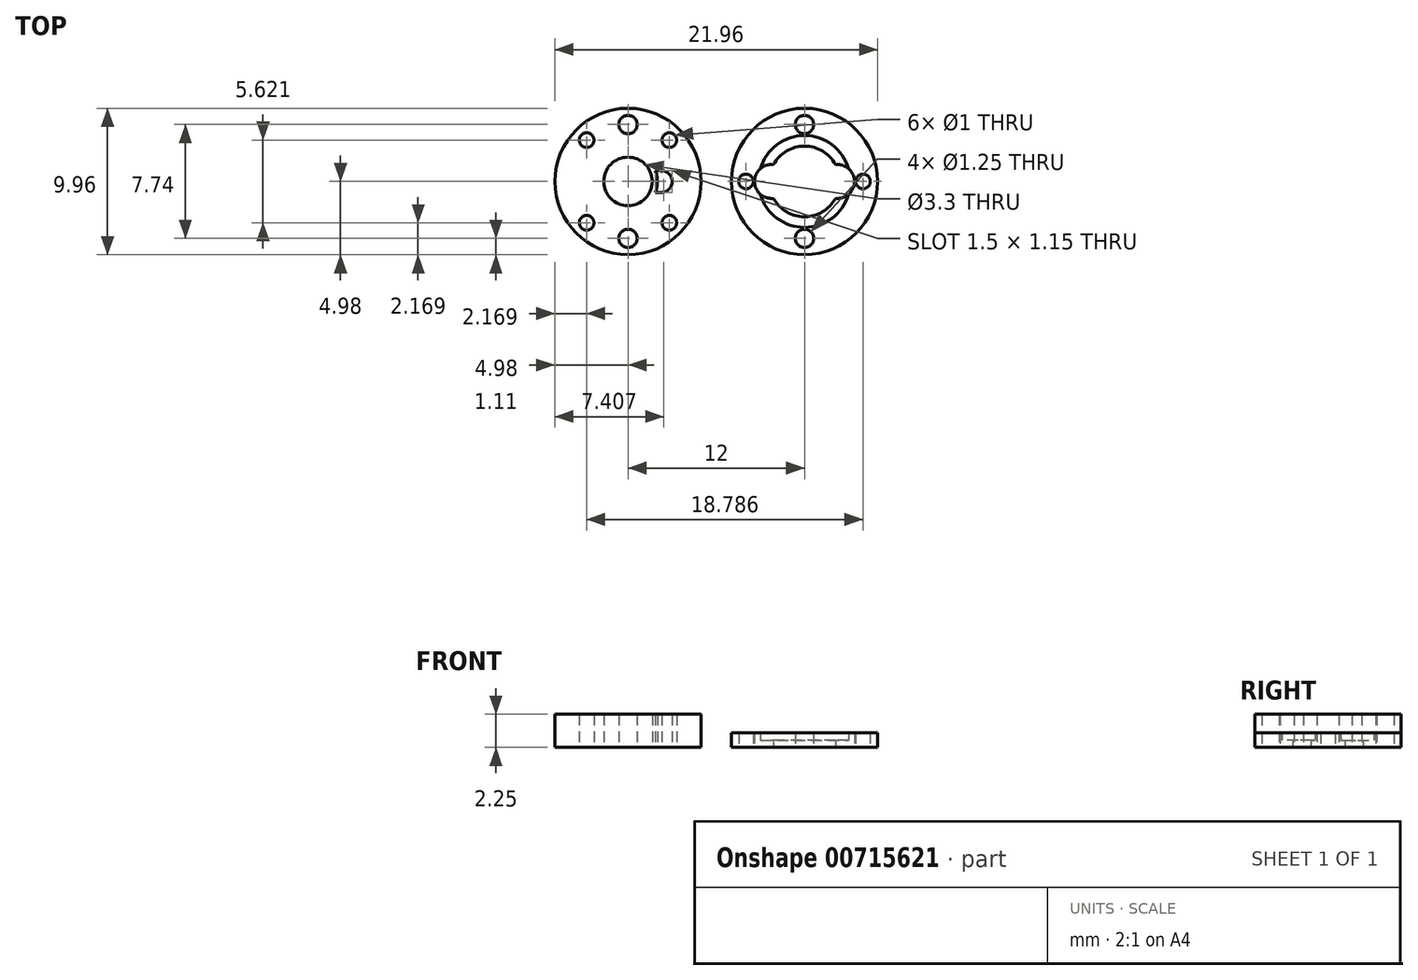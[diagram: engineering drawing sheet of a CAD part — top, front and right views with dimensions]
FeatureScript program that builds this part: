
annotation { "Feature Type Name" : "Feature", "Feature Type Description" : "" }
export const myFeature = defineFeature(function(context is Context, id is Id, definition is map)
    precondition{}
    {
        {
            var Q0;
            Q0=qCreatedBy(makeId("Top.planeOp"),FACE);
            var sketch = newSketch(context, id + "F0", { "sketchPlane" : qUnion([Q0])});
            skCircle(sketch, "E0", {"center": v(0, 0) * mm, "radius": 4.98 * mm});
            skCircle(sketch, "E1", {"center": v(0, 0) * mm, "radius": 1.65 * mm});
            skLineSegment(sketch, "E2", {"start": v(0, 0) * mm, "end": v(-3, 0) * mm, "construction": true});
            skLineSegment(sketch, "E3", {"start": v(0, 0.75) * mm, "end": v(0, 6.53) * mm, "construction": true});
            skLineSegment(sketch, "E4.bottom", {"start": v(-2.25, -0.75) * mm, "end": v(-1.99, -0.75) * mm});
            skLineSegment(sketch, "E4.top", {"start": v(-2.25, 0.75) * mm, "end": v(-1.99, 0.75) * mm});
            skLineSegment(sketch, "E4.left", {"start": v(-3, 0) * mm, "end": v(-3, 0) * mm});
            skLineSegment(sketch, "E4.right", {"start": v(0, 0) * mm, "end": v(0, 0.75) * mm});
            skPoint(sketch, "E4.middle", {"position": v(-1.5, 0) * mm});
            skPoint(sketch, "E5.orphan", {"position": v(0, -0.75) * mm});
            skPoint(sketch, "E6.visualSharp", {"position": v(-3, 0.75) * mm});
            skArc(sketch, "E6.filletArc", {"start": v(-2.25, 0.75) * mm, "mid": v(-2.78, 0.53) * mm, "end": v(-3, 0) * mm});
            skPoint(sketch, "E7.visualSharp", {"position": v(-3, -0.75) * mm});
            skArc(sketch, "E7.filletArc", {"start": v(-3, 0) * mm, "mid": v(-2.78, -0.53) * mm, "end": v(-2.25, -0.75) * mm});
            skArc(sketch, "E8.MirrorCS", {"start": v(3, 0) * mm, "mid": v(2.78, -0.53) * mm, "end": v(2.25, -0.75) * mm});
            skLineSegment(sketch, "E9.MirrorCS", {"start": v(2.25, -0.75) * mm, "end": v(1.99, -0.75) * mm});
            skArc(sketch, "E10.MirrorCS", {"start": v(2.25, 0.75) * mm, "mid": v(2.78, 0.53) * mm, "end": v(3, 0) * mm});
            skLineSegment(sketch, "E11.MirrorCS", {"start": v(2.25, 0.75) * mm, "end": v(1.99, 0.75) * mm});
            skLineSegment(sketch, "E12", {"start": v(0, 4.98) * mm, "end": v(0, 3.87) * mm, "construction": true});
            skCircle(sketch, "E13", {"center": v(0, 3.87) * mm, "radius": 0.62 * mm});
            skCircle(sketch, "E14.1.0", {"center": v(0, -3.87) * mm, "radius": 0.62 * mm});
            skLineSegment(sketch, "E15", {"start": v(0, 0) * mm, "end": v(-3.52, 3.52) * mm, "construction": true});
            skLineSegment(sketch, "E16", {"start": v(-3.52, 3.52) * mm, "end": v(-2.81, 2.81) * mm, "construction": true});
            skCircle(sketch, "E17", {"center": v(-2.81, 2.81) * mm, "radius": 0.5 * mm});
            skLineSegment(sketch, "E18.MirrorCS", {"start": v(0, 0) * mm, "end": v(-3.52, -3.52) * mm, "construction": true});
            skCircle(sketch, "E19.MirrorC", {"center": v(-2.81, -2.81) * mm, "radius": 0.5 * mm});
            skLineSegment(sketch, "E20.MirrorCS", {"start": v(-3.52, -3.52) * mm, "end": v(-2.81, -2.81) * mm, "construction": true});
            skCircle(sketch, "E21.MirrorC", {"center": v(2.81, 2.81) * mm, "radius": 0.5 * mm});
            skCircle(sketch, "E22.MirrorC", {"center": v(2.81, -2.81) * mm, "radius": 0.5 * mm});
            skLineSegment(sketch, "E23", {"start": v(0, 0) * mm, "end": v(12, 0) * mm, "construction": true});
            skCircle(sketch, "E24", {"center": v(12, 0) * mm, "radius": 4.97 * mm});
            skArc(sketch, "E25", {"start": v(10.15, -0.75) * mm, "mid": v(12, -2) * mm, "end": v(13.85, -0.75) * mm, "construction": true});
            skCircle(sketch, "E26", {"center": v(12, 0) * mm, "radius": 3.12 * mm});
            skLineSegment(sketch, "E27", {"start": v(12, 0) * mm, "end": v(15, 0) * mm, "construction": true});
            skLineSegment(sketch, "E28.bottom", {"start": v(13.85, -0.75) * mm, "end": v(14.25, -0.75) * mm, "construction": true});
            skLineSegment(sketch, "E28.top", {"start": v(13.85, 0.75) * mm, "end": v(14.25, 0.75) * mm, "construction": true});
            skLineSegment(sketch, "E28.left", {"start": v(12, -0.75) * mm, "end": v(12, 0.75) * mm});
            skLineSegment(sketch, "E28.right", {"start": v(15, -0.75) * mm, "end": v(15, 0) * mm, "construction": true});
            skPoint(sketch, "E28.middle", {"position": v(13.5, 0) * mm});
            skPoint(sketch, "E29.visualSharp", {"position": v(15, 0.75) * mm});
            skArc(sketch, "E29.filletArc", {"start": v(15, 0) * mm, "mid": v(14.78, 0.53) * mm, "end": v(14.25, 0.75) * mm, "construction": true});
            skArc(sketch, "E30.MirrorCS", {"start": v(15, 0) * mm, "mid": v(14.78, -0.53) * mm, "end": v(14.25, -0.75) * mm, "construction": true});
            skLineSegment(sketch, "E31.MirrorCS", {"start": v(10.15, -0.75) * mm, "end": v(9.75, -0.75) * mm, "construction": true});
            skArc(sketch, "E32.MirrorCS", {"start": v(9, 0) * mm, "mid": v(9.22, -0.53) * mm, "end": v(9.75, -0.75) * mm, "construction": true});
            skArc(sketch, "E33.MirrorCS", {"start": v(9, 0) * mm, "mid": v(9.22, 0.53) * mm, "end": v(9.75, 0.75) * mm, "construction": true});
            skLineSegment(sketch, "E34.MirrorCS", {"start": v(10.15, 0.75) * mm, "end": v(9.75, 0.75) * mm, "construction": true});
            skArc(sketch, "E35.trimOffspring", {"start": v(13.85, 0.75) * mm, "mid": v(12, 2) * mm, "end": v(10.15, 0.75) * mm, "construction": true});
            skLineSegment(sketch, "E36.0", {"start": v(14.1, 1.15) * mm, "end": v(14.25, 1.15) * mm});
            skArc(sketch, "E36.1", {"start": v(15.4, 0) * mm, "mid": v(15.06, 0.81) * mm, "end": v(14.25, 1.15) * mm});
            skArc(sketch, "E36.2", {"start": v(14.1, 1.15) * mm, "mid": v(12, 2.4) * mm, "end": v(9.9, 1.15) * mm});
            skArc(sketch, "E36.3", {"start": v(15.4, 0) * mm, "mid": v(15.06, -0.81) * mm, "end": v(14.25, -1.15) * mm});
            skLineSegment(sketch, "E36.4", {"start": v(14.1, -1.15) * mm, "end": v(14.25, -1.15) * mm});
            skArc(sketch, "E36.5", {"start": v(9.9, -1.15) * mm, "mid": v(12, -2.4) * mm, "end": v(14.1, -1.15) * mm});
            skLineSegment(sketch, "E36.6", {"start": v(9.9, 1.15) * mm, "end": v(9.75, 1.15) * mm});
            skArc(sketch, "E36.7", {"start": v(8.6, 0) * mm, "mid": v(8.94, 0.81) * mm, "end": v(9.75, 1.15) * mm});
            skArc(sketch, "E36.8", {"start": v(8.6, 0) * mm, "mid": v(8.94, -0.81) * mm, "end": v(9.75, -1.15) * mm});
            skLineSegment(sketch, "E36.9", {"start": v(9.9, -1.15) * mm, "end": v(9.75, -1.15) * mm});
            skLineSegment(sketch, "E37", {"start": v(12, 4.97) * mm, "end": v(12, 3.87) * mm, "construction": true});
            skCircle(sketch, "E38", {"center": v(12, 3.87) * mm, "radius": 0.62 * mm});
            skCircle(sketch, "E39.MirrorC", {"center": v(12, -3.87) * mm, "radius": 0.62 * mm});
            skLineSegment(sketch, "E40", {"start": v(12, 0) * mm, "end": v(7.03, 0) * mm, "construction": true});
            skLineSegment(sketch, "E41", {"start": v(7.03, 0) * mm, "end": v(8.03, 0) * mm, "construction": true});
            skCircle(sketch, "E42", {"center": v(8.03, 0) * mm, "radius": 0.5 * mm});
            skCircle(sketch, "E43.MirrorC", {"center": v(15.97, 0) * mm, "radius": 0.5 * mm});
            skCircle(sketch, "E44", {"center": v(0, 0) * mm, "radius": 2 * mm});
            skLineSegment(sketch, "E45", {"start": v(-2.25, 0.75) * mm, "end": v(-1.85, 0.75) * mm});
            skLineSegment(sketch, "E46", {"start": v(-2.25, -0.75) * mm, "end": v(-1.85, -0.75) * mm});
            skLineSegment(sketch, "E47", {"start": v(2.25, -0.75) * mm, "end": v(1.85, -0.75) * mm});
            skLineSegment(sketch, "E48", {"start": v(2.25, 0.75) * mm, "end": v(1.85, 0.75) * mm});
            skSolve(sketch);
        }
        {
            var Q0;
            Q0=makeQuery(id+"F0.imprint","IMPRINT",FACE,{"disambiguationData":[TD([[makeQuery(id+"F0.imprint","IMPRINT",EDGE,{"derivedFrom":sQuery(id+"F0.wireOp",EDGE,"E0")}),1.0]])]});
            extrude(context, id + "F1", {"entities" : qUnion([Q0]), "depth" : 1 * mm, "offsetDistance" : 25 * mm});
        }
        {
            var Q0;
            Q0=makeQuery(id+"F0.imprint","IMPRINT",FACE,{"disambiguationData":[TD([[makeQuery(id+"F0.imprint","IMPRINT",EDGE,{"derivedFrom":sQuery(id+"F0.wireOp",EDGE,"E8.MirrorCS")}),-1.0]])]});
            var Q1;
            Q1=makeQuery(id+"F0.imprint","IMPRINT",FACE,{"disambiguationData":[TD([[makeQuery(id+"F0.imprint","IMPRINT",EDGE,{"derivedFrom":sQuery(id+"F0.wireOp",EDGE,"E1")}),-1.0]])]});
            var Q2;
            {var subQ1=sQuery(id+"F0.wireOp",EDGE,"E4.bottom");Q2=makeQuery(id+"F0.imprint","IMPRINT",FACE,{"disambiguationData":[TD([[makeQuery(id+"F0.imprint","IMPRINT",EDGE,{"derivedFrom":subQ1}),1.0]])]});}
            var Q3;
            {var subQ1=sQuery(id+"F0.wireOp",EDGE,"E6.filletArc");Q3=makeQuery(id+"F0.imprint","IMPRINT",FACE,{"disambiguationData":[TD([[makeQuery(id+"F0.imprint","IMPRINT",EDGE,{"derivedFrom":subQ1}),1.0]])]});}
            extrude(context, id + "F2", {"entities" : qUnion([Q0, Q1, Q2, Q3]), "operationType" : NewBodyOperationType.ADD, "depth" : 2.25 * mm, "offsetDistance" : 25 * mm});
        }
        {
            var Q0;
            Q0=makeQuery(id+"F0.imprint","IMPRINT",FACE,{"disambiguationData":[TD([[makeQuery(id+"F0.imprint","IMPRINT",EDGE,{"derivedFrom":sQuery(id+"F0.wireOp",EDGE,"E24")}),1.0]])]});
            extrude(context, id + "F3", {"entities" : qUnion([Q0]), "depth" : 1 * mm, "offsetDistance" : 25 * mm});
        }
        {
            var Q0;
            {var subQ0=sQuery(id+"F0.wireOp",EDGE,"E36.4");Q0=makeQuery(id+"F0.imprint","IMPRINT",FACE,{"disambiguationData":[TD([[makeQuery(id+"F0.imprint","IMPRINT",EDGE,{"derivedFrom":subQ0}),-1.0]])]});}
            var Q1;
            {var subQ1=sQuery(id+"F0.wireOp",EDGE,"E36.0");Q1=makeQuery(id+"F0.imprint","IMPRINT",FACE,{"disambiguationData":[TD([[makeQuery(id+"F0.imprint","IMPRINT",EDGE,{"derivedFrom":subQ1}),1.0]])]});}
            extrude(context, id + "F4", {"entities" : qUnion([Q0, Q1]), "operationType" : NewBodyOperationType.ADD, "depth" : .5 * mm, "offsetDistance" : 25 * mm});
        }
    });
